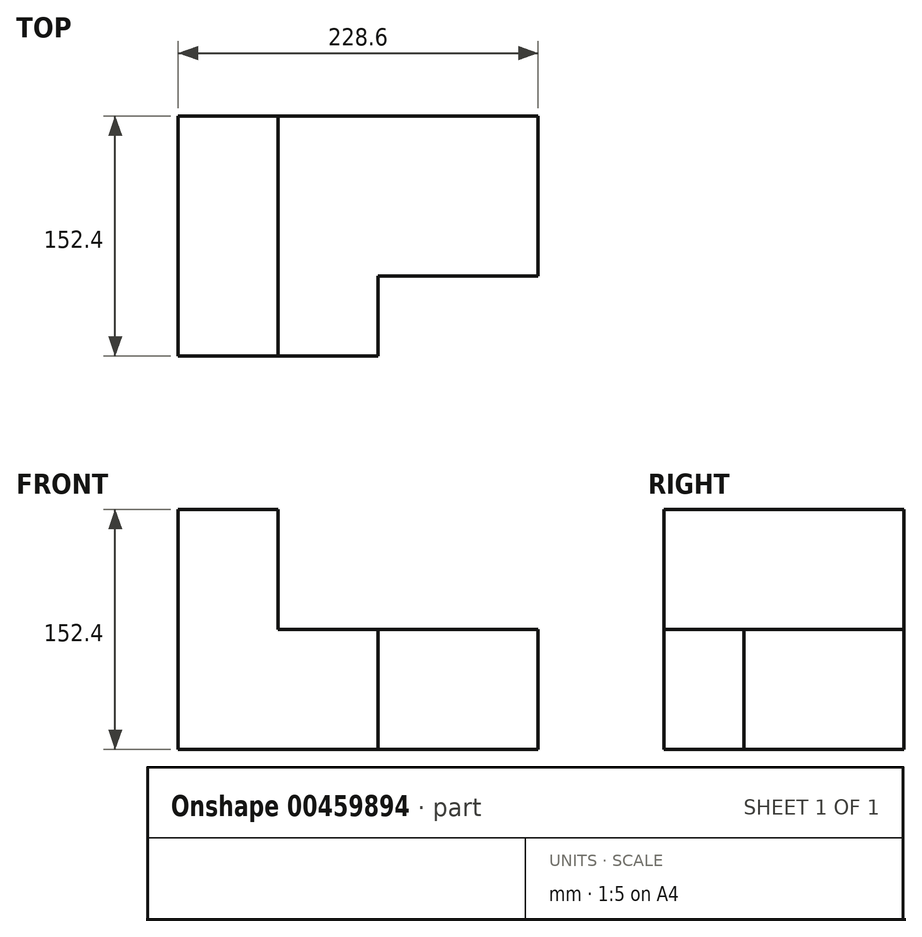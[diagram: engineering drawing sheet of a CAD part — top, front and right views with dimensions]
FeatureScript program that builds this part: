
annotation { "Feature Type Name" : "Feature", "Feature Type Description" : "" }
export const myFeature = defineFeature(function(context is Context, id is Id, definition is map)
    precondition{}
    {
        {
            var Q0;
            Q0=qCreatedBy(makeId("Front.planeOp"),FACE);
            var sketch = newSketch(context, id + "F0", { "sketchPlane" : qUnion([Q0])});
            skLineSegment(sketch, "E0", {"start": v(0, 0) * mm, "end": v(-228.6, 0) * mm});
            skLineSegment(sketch, "E1", {"start": v(-228.6, 0) * mm, "end": v(-228.6, 152.4) * mm});
            skLineSegment(sketch, "E2", {"start": v(-228.6, 152.4) * mm, "end": v(-165.1, 152.4) * mm});
            skLineSegment(sketch, "E3", {"start": v(-165.1, 152.4) * mm, "end": v(-165.1, 76.2) * mm});
            skLineSegment(sketch, "E4", {"start": v(-165.1, 76.2) * mm, "end": v(0, 76.2) * mm});
            skLineSegment(sketch, "E5", {"start": v(0, 76.2) * mm, "end": v(0, 0) * mm});
            skLineSegment(sketch, "E6", {"start": v(-101.6, 76.2) * mm, "end": v(-101.6, 0) * mm});
            skSolve(sketch);
        }
        {
            var Q0;
            Q0 = qSketchRegion(id + "F0", true);
            var Q1;
            {var subQ1=sQuery(id+"F0.wireOp",EDGE,"E1");Q1=makeQuery(id+"F0.imprint","IMPRINT",FACE,{"disambiguationData":[TD([[makeQuery(id+"F0.imprint","IMPRINT",EDGE,{"derivedFrom":subQ1}),-1.0]])]});}
            extrude(context, id + "F1", {"entities" : qUnion([Q0, Q1]), "depth" : 152.4 * mm});
        }
        {
            var Q0;
            Q0=makeQuery(id+"F1.opExtrude","CAP_FACE",FACE,{"disambiguationData":[OSD([sQuery(id+"F0.wireOp",EDGE,"E0"),sQuery(id+"F0.wireOp",EDGE,"E1"),sQuery(id+"F0.wireOp",EDGE,"E2"),sQuery(id+"F0.wireOp",EDGE,"E3"),sQuery(id+"F0.wireOp",EDGE,"E4"),sQuery(id+"F0.wireOp",EDGE,"E5")])],"isStart":false});
            var sketch = newSketch(context, id + "F2", { "sketchPlane" : qUnion([Q0])});
            skLineSegment(sketch, "E7", {"start": v(-101.6, 76.2) * mm, "end": v(-101.6, 0) * mm});
            skLineSegment(sketch, "E8", {"start": v(-101.6, 0) * mm, "end": v(0, 0) * mm});
            skSolve(sketch);
        }
        {
            var Q0;
            {var subQ0=sQuery(id+"F2.wireOp",EDGE,"E7");Q0=makeQuery(id+"F2.imprint","IMPRINT",FACE,{"disambiguationData":[TD([[makeQuery(id+"F2.imprint","IMPRINT",EDGE,{"derivedFrom":subQ0}),1.0]])]});}
            extrude(context, id + "F3", {"entities" : qUnion([Q0]), "operationType" : NewBodyOperationType.REMOVE, "oppositeDirection" : true, "depth" : 50.8 * mm});
        }
    });
